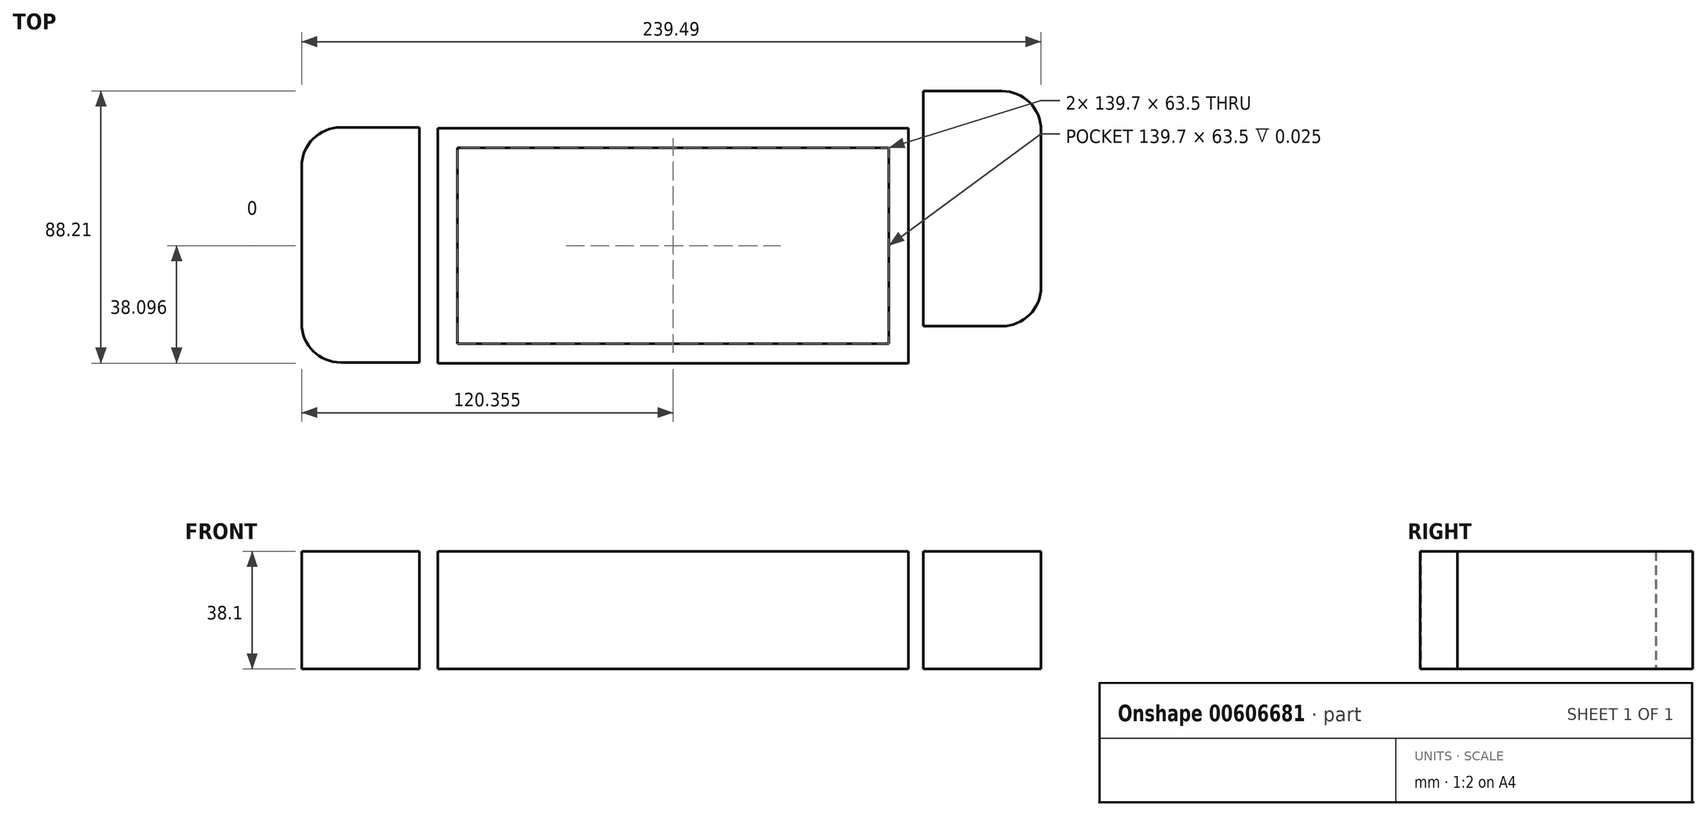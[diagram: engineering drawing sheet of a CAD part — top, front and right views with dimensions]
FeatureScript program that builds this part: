
annotation { "Feature Type Name" : "Feature", "Feature Type Description" : "" }
export const myFeature = defineFeature(function(context is Context, id is Id, definition is map)
    precondition{}
    {
        {
            var Q0;
            Q0=qCreatedBy(makeId("Top.planeOp"),FACE);
            var sketch = newSketch(context, id + "F0", { "sketchPlane" : qUnion([Q0])});
            skLineSegment(sketch, "E0.bottom", {"start": v(-131.82, 64.19) * mm, "end": v(20.58, 64.19) * mm});
            skLineSegment(sketch, "E0.top", {"start": v(-131.82, -12.01) * mm, "end": v(20.58, -12.01) * mm});
            skLineSegment(sketch, "E0.left", {"start": v(-131.82, 64.19) * mm, "end": v(-131.82, -12.01) * mm});
            skLineSegment(sketch, "E0.right", {"start": v(20.58, 64.19) * mm, "end": v(20.58, -12.01) * mm});
            skSolve(sketch);
        }
        {
            var Q0;
            Q0 = qSketchRegion(id + "F0", true);
            extrude(context, id + "F1", {"entities" : qUnion([Q0]), "depth" : 38.1 * mm, "offsetDistance" : 25.4 * mm});
        }
        {
            var Q0;
            Q0=qCreatedBy(makeId("Top.planeOp"),FACE);
            var sketch = newSketch(context, id + "F2", { "sketchPlane" : qUnion([Q0])});
            skLineSegment(sketch, "E1.bottom", {"start": v(25.42, 76.2) * mm, "end": v(50.82, 76.2) * mm});
            skLineSegment(sketch, "E1.top", {"start": v(25.42, 0) * mm, "end": v(50.82, 0) * mm});
            skLineSegment(sketch, "E1.left", {"start": v(25.42, 76.2) * mm, "end": v(25.42, 0) * mm});
            skLineSegment(sketch, "E1.right", {"start": v(63.52, 63.5) * mm, "end": v(63.52, 12.7) * mm});
            skPoint(sketch, "E2.visualSharp", {"position": v(63.52, 76.2) * mm});
            skArc(sketch, "E2.filletArc", {"start": v(63.52, 63.5) * mm, "mid": v(59.8, 72.48) * mm, "end": v(50.82, 76.2) * mm});
            skPoint(sketch, "E3.visualSharp", {"position": v(63.52, 0) * mm});
            skArc(sketch, "E3.filletArc", {"start": v(50.82, 0) * mm, "mid": v(59.8, 3.72) * mm, "end": v(63.52, 12.7) * mm});
            skSolve(sketch);
        }
        {
            var Q0;
            Q0=qCreatedBy(makeId("Top.planeOp"),FACE);
            var sketch = newSketch(context, id + "F3", { "sketchPlane" : qUnion([Q0])});
            skLineSegment(sketch, "E4.bottom", {"start": v(-163.27, 64.41) * mm, "end": v(-137.87, 64.41) * mm});
            skLineSegment(sketch, "E4.top", {"start": v(-163.27, -11.79) * mm, "end": v(-137.87, -11.79) * mm});
            skLineSegment(sketch, "E4.left", {"start": v(-175.97, 51.71) * mm, "end": v(-175.97, 0.91) * mm});
            skLineSegment(sketch, "E4.right", {"start": v(-137.87, 64.41) * mm, "end": v(-137.87, -11.79) * mm});
            skPoint(sketch, "E5.visualSharp", {"position": v(-175.97, 64.41) * mm});
            skArc(sketch, "E5.filletArc", {"start": v(-163.27, 64.41) * mm, "mid": v(-172.25, 60.7) * mm, "end": v(-175.97, 51.71) * mm});
            skPoint(sketch, "E6.visualSharp", {"position": v(-175.97, -11.79) * mm});
            skArc(sketch, "E6.filletArc", {"start": v(-175.97, 0.91) * mm, "mid": v(-172.25, -8.07) * mm, "end": v(-163.27, -11.79) * mm});
            skSolve(sketch);
        }
        {
            var Q0;
            Q0=makeQuery(id+"F3.imprint","IMPRINT",FACE,{"disambiguationData":[TD([[makeQuery(id+"F3.imprint","IMPRINT",EDGE,{"derivedFrom":sQuery(id+"F3.wireOp",EDGE,"E4.bottom")}),-1.0]])]});
            var Q1;
            Q1=makeQuery(id+"F2.imprint","IMPRINT",FACE,{"disambiguationData":[TD([[makeQuery(id+"F2.imprint","IMPRINT",EDGE,{"derivedFrom":sQuery(id+"F2.wireOp",EDGE,"E1.bottom")}),-1.0]])]});
            extrude(context, id + "F4", {"entities" : qUnion([Q0, Q1]), "depth" : 38.1 * mm, "offsetDistance" : 25.4 * mm});
        }
        {
            var Q0;
            Q0=makeQuery(id+"F1.opExtrude","CAP_FACE",FACE,{"disambiguationData":[OSD([sQuery(id+"F0.wireOp",EDGE,"E0.bottom"),sQuery(id+"F0.wireOp",EDGE,"E0.top"),sQuery(id+"F0.wireOp",EDGE,"E0.left"),sQuery(id+"F0.wireOp",EDGE,"E0.right")])],"isStart":false});
            var sketch = newSketch(context, id + "F5", { "sketchPlane" : qUnion([Q0])});
            skLineSegment(sketch, "E7.0", {"start": v(-125.47, 57.84) * mm, "end": v(14.23, 57.84) * mm});
            skLineSegment(sketch, "E7.1", {"start": v(-125.47, 57.84) * mm, "end": v(-125.47, -5.66) * mm});
            skLineSegment(sketch, "E7.2", {"start": v(-125.47, -5.66) * mm, "end": v(14.23, -5.66) * mm});
            skLineSegment(sketch, "E7.3", {"start": v(14.23, 57.84) * mm, "end": v(14.23, -5.66) * mm});
            skSolve(sketch);
        }
        {
            var Q0;
            Q0=makeQuery(id+"F5.imprint","IMPRINT",FACE,{"disambiguationData":[TD([[makeQuery(id+"F5.imprint","IMPRINT",EDGE,{"derivedFrom":sQuery(id+"F5.wireOp",EDGE,"E7.0")}),-1.0]])]});
            extrude(context, id + "F6", {"entities" : qUnion([Q0]), "operationType" : NewBodyOperationType.REMOVE, "oppositeDirection" : true, "depth" : 0.03 * mm, "offsetDistance" : 25.4 * mm});
        }
    });
